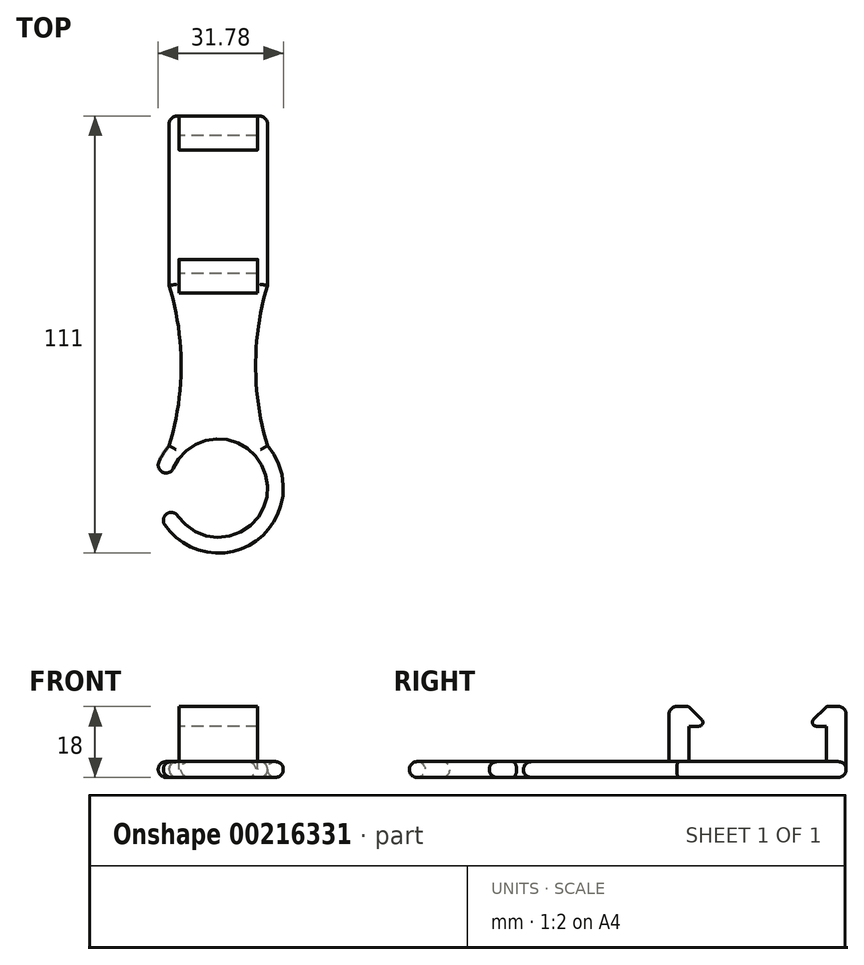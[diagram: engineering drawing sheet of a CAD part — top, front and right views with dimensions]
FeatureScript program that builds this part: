
annotation { "Feature Type Name" : "Feature", "Feature Type Description" : "" }
export const myFeature = defineFeature(function(context is Context, id is Id, definition is map)
    precondition{}
    {
        {
            var Q0;
            Q0=qCreatedBy(makeId("Top.planeOp"),FACE);
            var sketch = newSketch(context, id + "F0", { "sketchPlane" : qUnion([Q0])});
            skLineSegment(sketch, "E0.bottom", {"start": v(-10.5, 43) * mm, "end": v(10.5, 43) * mm});
            skLineSegment(sketch, "E0.top", {"start": v(-12.5, 0) * mm, "end": v(12.5, 0) * mm});
            skLineSegment(sketch, "E0.left", {"start": v(-12.5, 41) * mm, "end": v(-12.5, 0) * mm});
            skLineSegment(sketch, "E0.right", {"start": v(12.5, 41) * mm, "end": v(12.5, 0) * mm});
            skCircle(sketch, "E1", {"center": v(0, -51.5) * mm, "radius": 16.5 * mm});
            skArc(sketch, "E2", {"start": v(-12.5, -40.73) * mm, "mid": v(-9.47, -20.36) * mm, "end": v(-12.5, 0) * mm});
            skArc(sketch, "E3", {"start": v(12.5, 0) * mm, "mid": v(9.47, -20.36) * mm, "end": v(12.5, -40.73) * mm});
            skPoint(sketch, "E4.visualSharp", {"position": v(-12.5, 43) * mm});
            skArc(sketch, "E4.filletArc", {"start": v(-10.5, 43) * mm, "mid": v(-11.91, 42.41) * mm, "end": v(-12.5, 41) * mm});
            skPoint(sketch, "E5.visualSharp", {"position": v(12.5, 43) * mm});
            skArc(sketch, "E5.filletArc", {"start": v(12.5, 41) * mm, "mid": v(11.91, 42.41) * mm, "end": v(10.5, 43) * mm});
            skSolve(sketch);
        }
        {
            var Q0;
            Q0 = qSketchRegion(id + "F0", true);
            extrude(context, id + "F1", {"entities" : qUnion([Q0]), "depth" : 4 * mm});
        }
        {
            var Q0;
            Q0=qCreatedBy(makeId("Right.planeOp"),FACE);
            var sketch = newSketch(context, id + "F2", { "sketchPlane" : qUnion([Q0])});
            skLineSegment(sketch, "E6.bottom", {"start": v(43, 18) * mm, "end": v(38, 18) * mm});
            skLineSegment(sketch, "E6.top", {"start": v(43, 0) * mm, "end": v(38, 0) * mm});
            skLineSegment(sketch, "E6.left", {"start": v(43, 18) * mm, "end": v(43, 0) * mm});
            skLineSegment(sketch, "E6.right", {"start": v(38, 18) * mm, "end": v(38, 0) * mm});
            skLineSegment(sketch, "E7.bottom", {"start": v(-2, 18) * mm, "end": v(3, 18) * mm});
            skLineSegment(sketch, "E7.top", {"start": v(-2, 0) * mm, "end": v(3, 0) * mm});
            skLineSegment(sketch, "E7.left", {"start": v(-2, 18) * mm, "end": v(-2, 0) * mm});
            skLineSegment(sketch, "E7.right", {"start": v(3, 18) * mm, "end": v(3, 0) * mm});
            skLineSegment(sketch, "E8", {"start": v(38, 18) * mm, "end": v(33, 13) * mm});
            skLineSegment(sketch, "E9", {"start": v(33, 13) * mm, "end": v(38, 13) * mm});
            skLineSegment(sketch, "E10", {"start": v(3, 18) * mm, "end": v(8, 13) * mm});
            skLineSegment(sketch, "E11", {"start": v(8, 13) * mm, "end": v(3, 13) * mm});
            skSolve(sketch);
        }
        {
            var Q0;
            Q0 = qSketchRegion(id + "F2", true);
            extrude(context, id + "F3", {"entities" : qUnion([Q0]), "operationType" : NewBodyOperationType.ADD, "endBound" : BoundingType.SYMMETRIC, "depth" : 20 * mm});
        }
        {
            var Q0;
            Q0=qCreatedBy(makeId("Top.planeOp"),FACE);
            var sketch = newSketch(context, id + "F4", { "sketchPlane" : qUnion([Q0])});
            skCircle(sketch, "E12", {"center": v(0, -51.5) * mm, "radius": 12.5 * mm});
            skLineSegment(sketch, "E13", {"start": v(-11.9, -47.68) * mm, "end": v(-19.07, -47.68) * mm});
            skLineSegment(sketch, "E14", {"start": v(-19.07, -47.68) * mm, "end": v(-19.07, -57.68) * mm});
            skLineSegment(sketch, "E15", {"start": v(-19.07, -57.68) * mm, "end": v(-10.87, -57.68) * mm});
            skSolve(sketch);
        }
        {
            var Q0;
            Q0 = qSketchRegion(id + "F4", true);
            extrude(context, id + "F5", {"entities" : qUnion([Q0]), "operationType" : NewBodyOperationType.REMOVE, "endBound" : BoundingType.SYMMETRIC, "depth" : 14.6 * mm});
        }
        {
            var Q0;
            Q0=makeQuery(id+"F3.boolean.opBoolean","MERGE",EDGE,{"derivedFrom":[makeQuery(id+"F1.opExtrude","CAP_EDGE",EDGE,{"disambiguationData":[OSD([sQuery(id+"F0.wireOp",EDGE,"E0.left")])],"isStart":true}),makeQuery(id+"F3.opExtrude","CAP_EDGE",EDGE,{"disambiguationData":[OSD([sQuery(id+"F2.wireOp",EDGE,"E6.top")])],"isStart":true})]});
            var Q1;
            Q1=makeQuery(id+"F3.opExtrude","SWEPT_EDGE",EDGE,{"disambiguationData":[OSD([sQuery(id+"F2.wireOp",EDGE,"E6.bottom"),sQuery(id+"F2.wireOp",EDGE,"E6.left")])]});
            var Q2;
            Q2=makeQuery(id+"F3.opExtrude","SWEPT_EDGE",EDGE,{"disambiguationData":[OSD([sQuery(id+"F2.wireOp",EDGE,"E7.bottom"),sQuery(id+"F2.wireOp",EDGE,"E7.left")])]});
            var Q3;
            Q3=makeQuery(id+"F3.boolean.opBoolean","MERGE",EDGE,{"derivedFrom":[makeQuery(id+"F1.opExtrude","CAP_EDGE",EDGE,{"disambiguationData":[OSD([sQuery(id+"F0.wireOp",EDGE,"E0.right")])],"isStart":true}),makeQuery(id+"F3.opExtrude","CAP_EDGE",EDGE,{"disambiguationData":[OSD([sQuery(id+"F2.wireOp",EDGE,"E6.top")])],"isStart":false})]});
            var Q4;
            Q4=makeQuery(id+"F1.opExtrude","CAP_EDGE",EDGE,{"disambiguationData":[OSD([sQuery(id+"F0.wireOp",EDGE,"E2")])],"isStart":true});
            var Q5;
            Q5=makeQuery(id+"F1.opExtrude","CAP_EDGE",EDGE,{"disambiguationData":[OSD([sQuery(id+"F0.wireOp",EDGE,"E3")])],"isStart":true});
            var Q6;
            Q6=makeQuery(id+"F1.opExtrude","CAP_EDGE",EDGE,{"disambiguationData":[OSD([sQuery(id+"F0.wireOp",EDGE,"E3")])],"isStart":false});
            var Q7;
            Q7=makeQuery(id+"F1.opExtrude","CAP_EDGE",EDGE,{"disambiguationData":[OSD([sQuery(id+"F0.wireOp",EDGE,"E2")])],"isStart":false});
            var Q8;
            Q8=makeQuery(id+"F1.opExtrude","CAP_EDGE",EDGE,{"disambiguationData":[OSD([sQuery(id+"F0.wireOp",EDGE,"E0.right")])],"isStart":false});
            var Q9;
            Q9=makeQuery(id+"F1.opExtrude","CAP_EDGE",EDGE,{"disambiguationData":[OSD([sQuery(id+"F0.wireOp",EDGE,"E0.left")])],"isStart":false});
            fillet(context, id + "F6", {"entities" : qUnion([Q0, Q1, Q2, Q3, Q4, Q5, Q6, Q7, Q8, Q9]), "radius" : 2 * mm, "tangentPropagation" : true, "allowEdgeOverflow" : false});
        }
        {
            var Q0;
            Q0=makeQuery(id+"F5.boolean.opBoolean","INTERSECT",EDGE,{"derivedFrom":[makeQuery(id+"F1.opExtrude","CAP_FACE",FACE,{"disambiguationData":[OSD([sQuery(id+"F0.wireOp",EDGE,"E0.bottom"),sQuery(id+"F0.wireOp",EDGE,"E0.left"),sQuery(id+"F0.wireOp",EDGE,"E0.right"),sQuery(id+"F0.wireOp",EDGE,"E1"),sQuery(id+"F0.wireOp",EDGE,"E2"),sQuery(id+"F0.wireOp",EDGE,"E3"),sQuery(id+"F0.wireOp",EDGE,"E4.filletArc"),sQuery(id+"F0.wireOp",EDGE,"E5.filletArc")])],"isStart":true}),makeQuery(id+"F5.opExtrude","SWEPT_FACE",FACE,{"disambiguationData":[OSD([sQuery(id+"F4.wireOp",EDGE,"E12")])]})]});
            var Q1;
            Q1=makeQuery(id+"F5.boolean.opBoolean","INTERSECT",EDGE,{"derivedFrom":[makeQuery(id+"F1.opExtrude","CAP_FACE",FACE,{"disambiguationData":[OSD([sQuery(id+"F0.wireOp",EDGE,"E0.bottom"),sQuery(id+"F0.wireOp",EDGE,"E0.left"),sQuery(id+"F0.wireOp",EDGE,"E0.right"),sQuery(id+"F0.wireOp",EDGE,"E1"),sQuery(id+"F0.wireOp",EDGE,"E2"),sQuery(id+"F0.wireOp",EDGE,"E3"),sQuery(id+"F0.wireOp",EDGE,"E4.filletArc"),sQuery(id+"F0.wireOp",EDGE,"E5.filletArc")])],"isStart":false}),makeQuery(id+"F5.opExtrude","SWEPT_FACE",FACE,{"disambiguationData":[OSD([sQuery(id+"F4.wireOp",EDGE,"E12")])]})]});
            var Q2;
            Q2=makeQuery(id+"F5.boolean.opBoolean","INTERSECT",EDGE,{"derivedFrom":[makeQuery(id+"F1.opExtrude","SWEPT_FACE",FACE,{"disambiguationData":[OSD([sQuery(id+"F0.wireOp",EDGE,"E1")])]}),makeQuery(id+"F5.opExtrude","SWEPT_FACE",FACE,{"disambiguationData":[OSD([sQuery(id+"F4.wireOp",EDGE,"i8GsE9ai-5UMk-WxIP-9yrL-V24oocNDVq6Q")])]})]});
            var Q3;
            Q3=makeQuery(id+"F5.boolean.opBoolean","COPY",FACE,{"derivedFrom":makeQuery(id+"F5.opExtrude","SWEPT_FACE",FACE,{"disambiguationData":[OSD([sQuery(id+"F4.wireOp",EDGE,"i8GsE9ai-5UMk-WxIP-9yrL-V24oocNDVq6Q")])]})});
            var Q4;
            Q4=makeQuery(id+"F5.boolean.opBoolean","COPY",FACE,{"derivedFrom":makeQuery(id+"F5.opExtrude","SWEPT_FACE",FACE,{"disambiguationData":[OSD([sQuery(id+"F4.wireOp",EDGE,"0JrKTBnR-xOEm-1JNl-37gt-DNZAQ6REPkpy")])]})});
            var Q5;
            Q5=makeQuery(id+"F1.opExtrude","CAP_EDGE",EDGE,{"disambiguationData":[OSD([sQuery(id+"F0.wireOp",EDGE,"E1")])],"isStart":false});
            var Q6;
            Q6=makeQuery(id+"F1.opExtrude","CAP_EDGE",EDGE,{"disambiguationData":[OSD([sQuery(id+"F0.wireOp",EDGE,"E1")])],"isStart":true});
            var Q7;
            Q7=makeQuery(id+"F5.boolean.opBoolean","COPY",EDGE,{"derivedFrom":makeQuery(id+"F5.opExtrude","SWEPT_EDGE",EDGE,{"disambiguationData":[OSD([sQuery(id+"F4.wireOp",EDGE,"E12"),sQuery(id+"F4.wireOp",EDGE,"E13")])]})});
            var Q8;
            Q8=makeQuery(id+"F5.boolean.opBoolean","COPY",EDGE,{"derivedFrom":makeQuery(id+"F5.opExtrude","SWEPT_EDGE",EDGE,{"disambiguationData":[OSD([sQuery(id+"F4.wireOp",EDGE,"E12"),sQuery(id+"F4.wireOp",EDGE,"E15")])]})});
            var Q9;
            Q9=makeQuery(id+"F5.boolean.opBoolean","COPY",FACE,{"derivedFrom":makeQuery(id+"F5.opExtrude","SWEPT_FACE",FACE,{"disambiguationData":[OSD([sQuery(id+"F4.wireOp",EDGE,"E13")])]})});
            var Q10;
            Q10=makeQuery(id+"F5.boolean.opBoolean","COPY",FACE,{"derivedFrom":makeQuery(id+"F5.opExtrude","SWEPT_FACE",FACE,{"disambiguationData":[OSD([sQuery(id+"F4.wireOp",EDGE,"E15")])]})});
            fillet(context, id + "F7", {"entities" : qUnion([Q0, Q1, Q2, Q3, Q4, Q5, Q6, Q7, Q8, Q9, Q10]), "radius" : 2 * mm, "tangentPropagation" : true, "allowEdgeOverflow" : false});
        }
        {
            var Q0;
            Q0=makeQuery(id+"F3.opExtrude","SWEPT_EDGE",EDGE,{"disambiguationData":[OSD([sQuery(id+"F2.wireOp",EDGE,"E8"),sQuery(id+"F2.wireOp",EDGE,"E9")])]});
            var Q1;
            Q1=makeQuery(id+"F3.opExtrude","SWEPT_EDGE",EDGE,{"disambiguationData":[OSD([sQuery(id+"F2.wireOp",EDGE,"E10"),sQuery(id+"F2.wireOp",EDGE,"E11")])]});
            var Q2;
            Q2=makeQuery(id+"F3.opExtrude","SWEPT_EDGE",EDGE,{"disambiguationData":[OSD([sQuery(id+"F2.wireOp",EDGE,"E7.bottom"),sQuery(id+"F2.wireOp",EDGE,"E7.right"),sQuery(id+"F2.wireOp",EDGE,"E10")])]});
            var Q3;
            Q3=makeQuery(id+"F3.opExtrude","SWEPT_EDGE",EDGE,{"disambiguationData":[OSD([sQuery(id+"F2.wireOp",EDGE,"E6.bottom"),sQuery(id+"F2.wireOp",EDGE,"E6.right"),sQuery(id+"F2.wireOp",EDGE,"E8")])]});
            fillet(context, id + "F8", {"entities" : qUnion([Q0, Q1, Q2, Q3]), "radius" : 1 * mm, "tangentPropagation" : true, "allowEdgeOverflow" : false});
        }
    });
